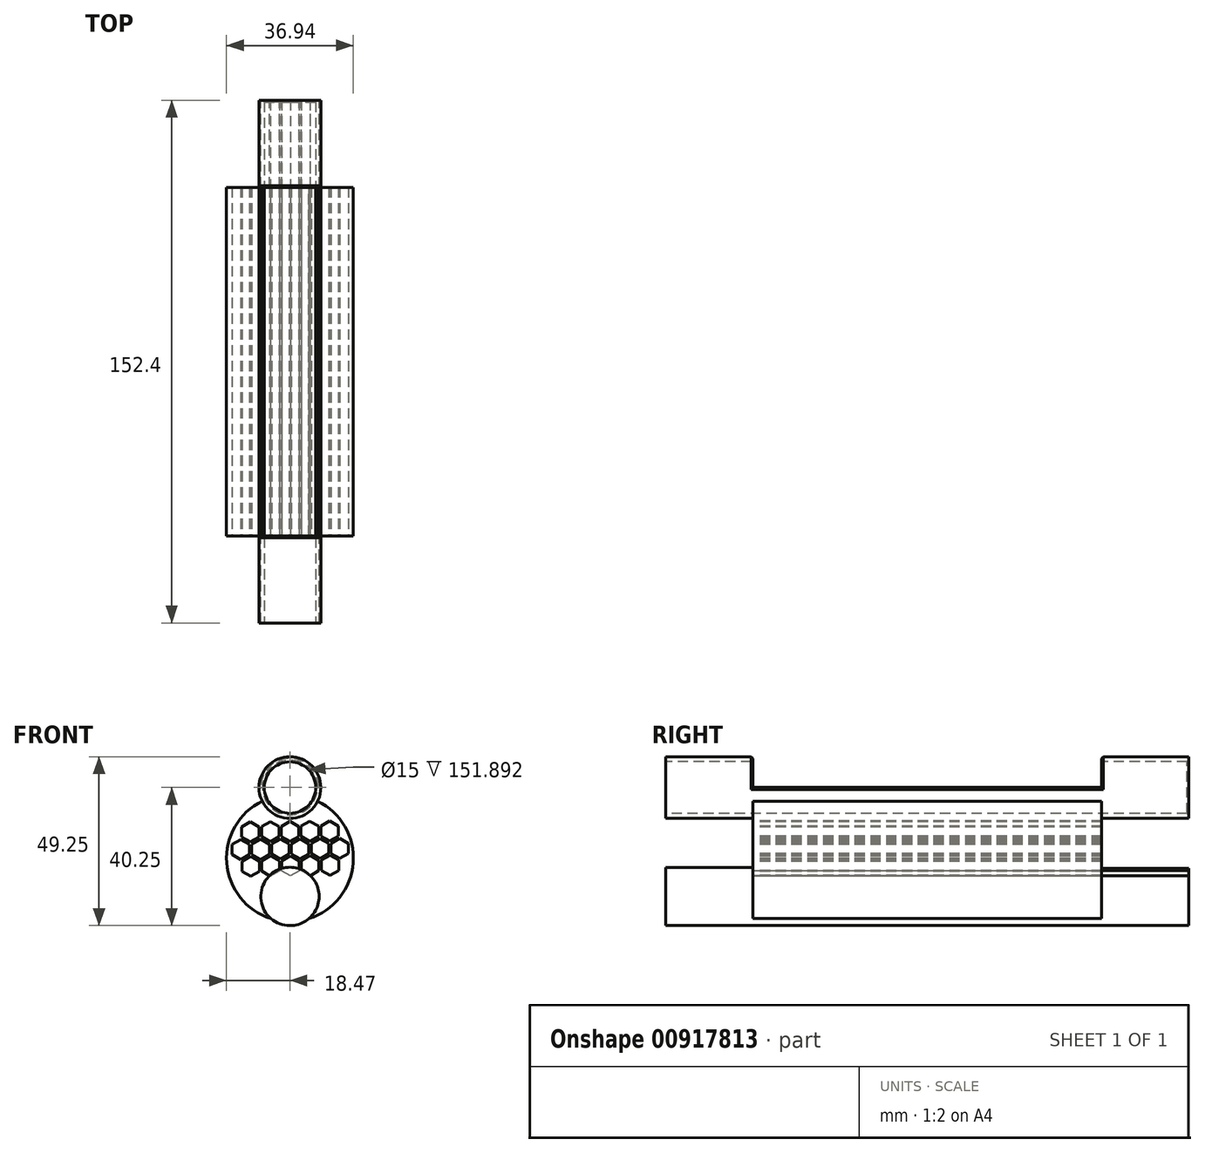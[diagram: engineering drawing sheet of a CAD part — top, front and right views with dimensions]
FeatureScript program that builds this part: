
annotation { "Feature Type Name" : "Feature", "Feature Type Description" : "" }
export const myFeature = defineFeature(function(context is Context, id is Id, definition is map)
    precondition{}
    {
        {
            var Q0;
            Q0=qCreatedBy(makeId("Front.planeOp"),FACE);
            var sketch = newSketch(context, id + "F0", { "sketchPlane" : qUnion([Q0])});
            skCircle(sketch, "E0", {"center": v(0, 0) * mm, "radius": 9 * mm});
            skCircle(sketch, "E1", {"center": v(0, -31.75) * mm, "radius": 8.5 * mm});
            skSolve(sketch);
        }
        {
            var Q0;
            Q0 = qSketchRegion(id + "FUGsYxlSOq7sT89_0", true);
            var Q1;
            Q1=makeQuery(id+"F0.imprint","IMPRINT",FACE,{"disambiguationData":[TD([[makeQuery(id+"F0.imprint","IMPRINT",EDGE,{"derivedFrom":sQuery(id+"F0.wireOp",EDGE,"E0")}),1.0]])]});
            var Q2;
            Q2=makeQuery(id+"F0.imprint","IMPRINT",FACE,{"disambiguationData":[TD([[makeQuery(id+"F0.imprint","IMPRINT",EDGE,{"derivedFrom":sQuery(id+"F0.wireOp",EDGE,"E1")}),1.0]])]});
            extrude(context, id + "F1", {"entities" : qUnion([Q0, Q1, Q2]), "endBound" : BoundingType.SYMMETRIC, "depth" : 152.4 * mm, "offsetDistance" : 25.4 * mm});
        }
        {
            var Q0;
            Q0=makeQuery(id+"F1.opExtrude","CAP_FACE",FACE,{"disambiguationData":[OSD([sQuery(id+"F0.wireOp",EDGE,"E0")])],"isStart":false});
            var sketch = newSketch(context, id + "F2", { "sketchPlane" : qUnion([Q0])});
            skCircle(sketch, "E2", {"center": v(0, 0) * mm, "radius": 7.5 * mm});
            skSolve(sketch);
        }
        {
            var Q0;
            Q0 = qSketchRegion(id + "F2", true);
            extrude(context, id + "F3", {"entities" : qUnion([Q0]), "operationType" : NewBodyOperationType.REMOVE, "endBound" : BoundingType.THROUGH_ALL, "oppositeDirection" : true, "depth" : 25.4 * mm, "offsetDistance" : 25.4 * mm});
        }
        {
            var Q0;
            Q0=makeQuery(id+"F0.imprint","IMPRINT",FACE,{"disambiguationData":[TD([[makeQuery(id+"F0.imprint","IMPRINT",EDGE,{"derivedFrom":sQuery(id+"F0.wireOp",EDGE,"E0")}),1.0]])]});
            var sketch = newSketch(context, id + "F4", { "sketchPlane" : qUnion([Q0])});
            skLineSegment(sketch, "E3.bottom", {"start": v(-11.18, 12.2) * mm, "end": v(12.33, 12.2) * mm});
            skLineSegment(sketch, "E3.top", {"start": v(-11.18, 0) * mm, "end": v(12.33, 0) * mm});
            skLineSegment(sketch, "E3.left", {"start": v(-11.18, 12.2) * mm, "end": v(-11.18, 0) * mm});
            skLineSegment(sketch, "E3.right", {"start": v(12.33, 12.2) * mm, "end": v(12.33, 0) * mm});
            skSolve(sketch);
        }
        {
            var Q0;
            Q0 = qSketchRegion(id + "F4", true);
            extrude(context, id + "F5", {"entities" : qUnion([Q0]), "operationType" : NewBodyOperationType.REMOVE, "endBound" : BoundingType.SYMMETRIC, "oppositeDirection" : true, "depth" : 101.6 * mm, "offsetDistance" : 25.4 * mm});
        }
        {
            var Q0;
            Q0=makeQuery(id+"F5.boolean.opBoolean","INTERSECT",EDGE,{"disambiguationData":[OD(0.0)],"derivedFrom":[makeQuery(id+"F1.opExtrude","SWEPT_FACE",FACE,{"disambiguationData":[OSD([sQuery(id+"F0.wireOp",EDGE,"E0")])]}),makeQuery(id+"F5.opExtrude","SWEPT_FACE",FACE,{"disambiguationData":[OSD([sQuery(id+"F4.wireOp",EDGE,"E3.top")])]})]});
            var Q1;
            Q1=makeQuery(id+"F5.boolean.opBoolean","INTERSECT",EDGE,{"disambiguationData":[OD(1.0)],"derivedFrom":[makeQuery(id+"F1.opExtrude","SWEPT_FACE",FACE,{"disambiguationData":[OSD([sQuery(id+"F0.wireOp",EDGE,"E0")])]}),makeQuery(id+"F5.opExtrude","SWEPT_FACE",FACE,{"disambiguationData":[OSD([sQuery(id+"F4.wireOp",EDGE,"E3.top")])]})]});
            var Q2;
            Q2=makeQuery(id+"F5.boolean.opBoolean","INTERSECT",EDGE,{"disambiguationData":[OD(1.0)],"derivedFrom":[makeQuery(id+"F3.boolean.opBoolean","COPY",FACE,{"derivedFrom":makeQuery(id+"F3.opExtrude","SWEPT_FACE",FACE,{"disambiguationData":[OSD([sQuery(id+"F2.wireOp",EDGE,"E2")])]})}),makeQuery(id+"F5.opExtrude","SWEPT_FACE",FACE,{"disambiguationData":[OSD([sQuery(id+"F4.wireOp",EDGE,"E3.top")])]})]});
            var Q3;
            Q3=makeQuery(id+"F5.boolean.opBoolean","INTERSECT",EDGE,{"disambiguationData":[OD(0.0)],"derivedFrom":[makeQuery(id+"F3.boolean.opBoolean","COPY",FACE,{"derivedFrom":makeQuery(id+"F3.opExtrude","SWEPT_FACE",FACE,{"disambiguationData":[OSD([sQuery(id+"F2.wireOp",EDGE,"E2")])]})}),makeQuery(id+"F5.opExtrude","SWEPT_FACE",FACE,{"disambiguationData":[OSD([sQuery(id+"F4.wireOp",EDGE,"E3.top")])]})]});
            var Q4;
            Q4=makeQuery(id+"F5.boolean.opBoolean","INTERSECT",EDGE,{"derivedFrom":[makeQuery(id+"F1.opExtrude","SWEPT_FACE",FACE,{"disambiguationData":[OSD([sQuery(id+"F0.wireOp",EDGE,"E0")])]}),makeQuery(id+"F5.opExtrude","CAP_FACE",FACE,{"disambiguationData":[OSD([sQuery(id+"F4.wireOp",EDGE,"E3.bottom"),sQuery(id+"F4.wireOp",EDGE,"E3.top"),sQuery(id+"F4.wireOp",EDGE,"E3.left"),sQuery(id+"F4.wireOp",EDGE,"E3.right")])],"isStart":true})]});
            var Q5;
            Q5=makeQuery(id+"F5.boolean.opBoolean","INTERSECT",EDGE,{"derivedFrom":[makeQuery(id+"F1.opExtrude","SWEPT_FACE",FACE,{"disambiguationData":[OSD([sQuery(id+"F0.wireOp",EDGE,"E0")])]}),makeQuery(id+"F5.opExtrude","CAP_FACE",FACE,{"disambiguationData":[OSD([sQuery(id+"F4.wireOp",EDGE,"E3.bottom"),sQuery(id+"F4.wireOp",EDGE,"E3.top"),sQuery(id+"F4.wireOp",EDGE,"E3.left"),sQuery(id+"F4.wireOp",EDGE,"E3.right")])],"isStart":false})]});
            var Q6;
            Q6=makeQuery(id+"F5.boolean.opBoolean","INTERSECT",EDGE,{"derivedFrom":[makeQuery(id+"F3.boolean.opBoolean","COPY",FACE,{"derivedFrom":makeQuery(id+"F3.opExtrude","SWEPT_FACE",FACE,{"disambiguationData":[OSD([sQuery(id+"F2.wireOp",EDGE,"E2")])]})}),makeQuery(id+"F5.opExtrude","CAP_FACE",FACE,{"disambiguationData":[OSD([sQuery(id+"F4.wireOp",EDGE,"E3.bottom"),sQuery(id+"F4.wireOp",EDGE,"E3.top"),sQuery(id+"F4.wireOp",EDGE,"E3.left"),sQuery(id+"F4.wireOp",EDGE,"E3.right")])],"isStart":false})]});
            var Q7;
            Q7=makeQuery(id+"F5.boolean.opBoolean","INTERSECT",EDGE,{"derivedFrom":[makeQuery(id+"F3.boolean.opBoolean","COPY",FACE,{"derivedFrom":makeQuery(id+"F3.opExtrude","SWEPT_FACE",FACE,{"disambiguationData":[OSD([sQuery(id+"F2.wireOp",EDGE,"E2")])]})}),makeQuery(id+"F5.opExtrude","CAP_FACE",FACE,{"disambiguationData":[OSD([sQuery(id+"F4.wireOp",EDGE,"E3.bottom"),sQuery(id+"F4.wireOp",EDGE,"E3.top"),sQuery(id+"F4.wireOp",EDGE,"E3.left"),sQuery(id+"F4.wireOp",EDGE,"E3.right")])],"isStart":true})]});
            var Q8;
            Q8=makeQuery(id+"F3.boolean.opBoolean","INTERSECT",EDGE,{"derivedFrom":[makeQuery(id+"F1.opExtrude","CAP_FACE",FACE,{"disambiguationData":[OSD([sQuery(id+"F0.wireOp",EDGE,"E0")])],"isStart":true}),makeQuery(id+"F3.opExtrude","SWEPT_FACE",FACE,{"disambiguationData":[OSD([sQuery(id+"F2.wireOp",EDGE,"E2")])]})]});
            var Q9;
            Q9=makeQuery(id+"F3.boolean.opBoolean","COPY",EDGE,{"derivedFrom":makeQuery(id+"F3.opExtrude","CAP_EDGE",EDGE,{"disambiguationData":[OSD([sQuery(id+"F2.wireOp",EDGE,"E2")])],"isStart":true})});
            chamfer(context, id + "F6", {"entities" : qUnion([Q0, Q1, Q2, Q3, Q4, Q5, Q6, Q7, Q8, Q9]), "width" : 0.5 * mm, "tangentPropagation" : true});
        }
        {
            var Q0;
            Q0=qCreatedBy(makeId("Front.planeOp"),FACE);
            var sketch = newSketch(context, id + "F7", { "sketchPlane" : qUnion([Q0])});
            skLineSegment(sketch, "E4.0", {"start": v(2, -31.75) * mm, "end": v(2, -8.64) * mm});
            skLineSegment(sketch, "E5.0", {"start": v(-2, -31.75) * mm, "end": v(-2, -8.64) * mm});
            skPoint(sketch, "E6.start.orphan", {"position": v(0, -31.75) * mm});
            skLineSegment(sketch, "E7", {"start": v(-2, -31.75) * mm, "end": v(2, -31.75) * mm});
            skLineSegment(sketch, "E8", {"start": v(2, -8.64) * mm, "end": v(-2, -8.64) * mm});
            skSolve(sketch);
        }
        {
            var Q0;
            Q0 = qSketchRegion(id + "F7", true);
            extrude(context, id + "F8", {"entities" : qUnion([Q0]), "operationType" : NewBodyOperationType.ADD, "endBound" : BoundingType.SYMMETRIC, "oppositeDirection" : true, "depth" : 101.6 * mm, "offsetDistance" : 25.4 * mm});
        }
        {
            var Q0;
            Q0=qCreatedBy(makeId("Front.planeOp"),FACE);
            var sketch = newSketch(context, id + "F9", { "sketchPlane" : qUnion([Q0])});
            skCircle(sketch, "E9", {"center": v(0, -20.58) * mm, "radius": 18.47 * mm});
            skSolve(sketch);
        }
        {
            var Q0;
            Q0 = qSketchRegion(id + "F9", true);
            extrude(context, id + "F10", {"entities" : qUnion([Q0]), "operationType" : NewBodyOperationType.ADD, "endBound" : BoundingType.SYMMETRIC, "depth" : 101.6 * mm, "offsetDistance" : 25.4 * mm});
        }
        {
            var Q0;
            Q0=makeQuery(id+"F0.imprint","IMPRINT",FACE,{"disambiguationData":[TD([[makeQuery(id+"F0.imprint","IMPRINT",EDGE,{"derivedFrom":sQuery(id+"F0.wireOp",EDGE,"E0")}),1.0]])]});
            var sketch = newSketch(context, id + "F11", { "sketchPlane" : qUnion([Q0])});
            skCircle(sketch, "E10", {"center": v(0, 0) * mm, "radius": 7.5 * mm});
            skSolve(sketch);
        }
        {
            var Q0;
            Q0 = qSketchRegion(id + "F11", true);
            extrude(context, id + "F12", {"entities" : qUnion([Q0]), "operationType" : NewBodyOperationType.REMOVE, "endBound" : BoundingType.SYMMETRIC, "oppositeDirection" : true, "depth" : 152.4 * mm, "offsetDistance" : 25.4 * mm});
        }
        {
            var Q0;
            Q0=makeQuery(id+"F10.boolean.opBoolean","MERGE",FACE,{"derivedFrom":[makeQuery(id+"F8.opExtrude","CAP_FACE",FACE,{"disambiguationData":[OSD([sQuery(id+"F7.wireOp",EDGE,"E4.0"),sQuery(id+"F7.wireOp",EDGE,"E5.0"),sQuery(id+"F7.wireOp",EDGE,"E7"),sQuery(id+"F7.wireOp",EDGE,"E8")])],"isStart":true}),makeQuery(id+"F10.opExtrude","CAP_FACE",FACE,{"disambiguationData":[OSD([sQuery(id+"F9.wireOp",EDGE,"E9")])],"isStart":false})]});
            var sketch = newSketch(context, id + "F13", { "sketchPlane" : qUnion([Q0])});
            skCircle(sketch, "E11.cCircle", {"center": v(-11.52, -12.94) * mm, "radius": 2.55 * mm, "construction": true});
            skLineSegment(sketch, "E11.0", {"start": v(-8.97, -11.46) * mm, "end": v(-8.97, -14.4) * mm});
            skLineSegment(sketch, "E11.1", {"start": v(-8.97, -14.4) * mm, "end": v(-11.52, -15.88) * mm});
            skLineSegment(sketch, "E11.2", {"start": v(-11.52, -15.88) * mm, "end": v(-14.07, -14.4) * mm});
            skLineSegment(sketch, "E11.3", {"start": v(-14.07, -14.4) * mm, "end": v(-14.07, -11.46) * mm});
            skLineSegment(sketch, "E11.4", {"start": v(-14.07, -11.46) * mm, "end": v(-11.52, -10) * mm});
            skLineSegment(sketch, "E11.5", {"start": v(-11.52, -10) * mm, "end": v(-8.97, -11.46) * mm});
            skPoint(sketch, "E11.0.midPoint", {"position": v(-8.97, -12.94) * mm});
            skLineSegment(sketch, "E12.1.0.0", {"start": v(-5.75, -9.92) * mm, "end": v(-3.2, -11.4) * mm});
            skLineSegment(sketch, "E12.1.0.1", {"start": v(-8.3, -11.4) * mm, "end": v(-5.75, -9.92) * mm});
            skLineSegment(sketch, "E12.1.0.2", {"start": v(-8.3, -14.34) * mm, "end": v(-8.3, -11.4) * mm});
            skLineSegment(sketch, "E12.1.0.3", {"start": v(-5.75, -15.81) * mm, "end": v(-8.3, -14.34) * mm});
            skLineSegment(sketch, "E12.1.0.4", {"start": v(-3.2, -11.4) * mm, "end": v(-3.2, -14.34) * mm});
            skLineSegment(sketch, "E12.1.0.5", {"start": v(-3.2, -14.34) * mm, "end": v(-5.75, -15.81) * mm});
            skLineSegment(sketch, "E12.2.0.0", {"start": v(0.02, -9.85) * mm, "end": v(2.57, -11.33) * mm});
            skLineSegment(sketch, "E12.2.0.1", {"start": v(-2.53, -11.33) * mm, "end": v(0.02, -9.85) * mm});
            skLineSegment(sketch, "E12.2.0.2", {"start": v(-2.53, -14.27) * mm, "end": v(-2.53, -11.33) * mm});
            skLineSegment(sketch, "E12.2.0.3", {"start": v(0.02, -15.74) * mm, "end": v(-2.53, -14.27) * mm});
            skLineSegment(sketch, "E12.2.0.4", {"start": v(2.57, -11.33) * mm, "end": v(2.57, -14.27) * mm});
            skLineSegment(sketch, "E12.2.0.5", {"start": v(2.57, -14.27) * mm, "end": v(0.02, -15.74) * mm});
            skLineSegment(sketch, "E12.3.0.0", {"start": v(5.78, -9.79) * mm, "end": v(8.33, -11.26) * mm});
            skLineSegment(sketch, "E12.3.0.1", {"start": v(3.23, -11.26) * mm, "end": v(5.78, -9.79) * mm});
            skLineSegment(sketch, "E12.3.0.2", {"start": v(3.23, -14.2) * mm, "end": v(3.23, -11.26) * mm});
            skLineSegment(sketch, "E12.3.0.3", {"start": v(5.78, -15.67) * mm, "end": v(3.23, -14.2) * mm});
            skLineSegment(sketch, "E12.3.0.4", {"start": v(8.33, -11.26) * mm, "end": v(8.33, -14.2) * mm});
            skLineSegment(sketch, "E12.3.0.5", {"start": v(8.33, -14.2) * mm, "end": v(5.78, -15.67) * mm});
            skLineSegment(sketch, "E12.4.0.0", {"start": v(11.55, -9.72) * mm, "end": v(14.1, -11.19) * mm});
            skLineSegment(sketch, "E12.4.0.1", {"start": v(9, -11.19) * mm, "end": v(11.55, -9.72) * mm});
            skLineSegment(sketch, "E12.4.0.2", {"start": v(9, -14.13) * mm, "end": v(9, -11.19) * mm});
            skLineSegment(sketch, "E12.4.0.3", {"start": v(11.55, -15.6) * mm, "end": v(9, -14.13) * mm});
            skLineSegment(sketch, "E12.4.0.4", {"start": v(14.1, -11.19) * mm, "end": v(14.1, -14.13) * mm});
            skLineSegment(sketch, "E12.4.0.5", {"start": v(14.1, -14.13) * mm, "end": v(11.55, -15.6) * mm});
            skLineSegment(sketch, "E12.direction1", {"start": v(-11.52, -10) * mm, "end": v(-5.75, -9.92) * mm, "construction": true});
            skSolve(sketch);
        }
        {
            var Q0;
            Q0 = qSketchRegion(id + "F13", true);
            extrude(context, id + "F14", {"entities" : qUnion([Q0]), "operationType" : NewBodyOperationType.REMOVE, "oppositeDirection" : true, "depth" : 177.8 * mm, "offsetDistance" : 25.4 * mm});
        }
        {
            var Q0;
            Q0=makeQuery(id+"F10.boolean.opBoolean","MERGE",FACE,{"derivedFrom":[makeQuery(id+"F8.opExtrude","CAP_FACE",FACE,{"disambiguationData":[OSD([sQuery(id+"F7.wireOp",EDGE,"E4.0"),sQuery(id+"F7.wireOp",EDGE,"E5.0"),sQuery(id+"F7.wireOp",EDGE,"E7"),sQuery(id+"F7.wireOp",EDGE,"E8")])],"isStart":true}),makeQuery(id+"F10.opExtrude","CAP_FACE",FACE,{"disambiguationData":[OSD([sQuery(id+"F9.wireOp",EDGE,"E9")])],"isStart":false})]});
            var sketch = newSketch(context, id + "F15", { "sketchPlane" : qUnion([Q0])});
            skCircle(sketch, "E13.cCircle", {"center": v(-14.33, -18.09) * mm, "radius": 2.55 * mm, "construction": true});
            skLineSegment(sketch, "E13.0", {"start": v(-11.78, -16.61) * mm, "end": v(-11.78, -19.56) * mm});
            skLineSegment(sketch, "E13.1", {"start": v(-11.78, -19.56) * mm, "end": v(-14.33, -21.03) * mm});
            skLineSegment(sketch, "E13.2", {"start": v(-14.33, -21.03) * mm, "end": v(-16.88, -19.56) * mm});
            skLineSegment(sketch, "E13.3", {"start": v(-16.88, -19.56) * mm, "end": v(-16.88, -16.61) * mm});
            skLineSegment(sketch, "E13.4", {"start": v(-16.88, -16.61) * mm, "end": v(-14.33, -15.14) * mm});
            skLineSegment(sketch, "E13.5", {"start": v(-14.33, -15.14) * mm, "end": v(-11.78, -16.61) * mm});
            skPoint(sketch, "E13.0.midPoint", {"position": v(-11.78, -18.09) * mm});
            skLineSegment(sketch, "E14.1.0.0", {"start": v(-8.56, -15.07) * mm, "end": v(-6.01, -16.55) * mm});
            skLineSegment(sketch, "E14.1.0.1", {"start": v(-11.11, -16.55) * mm, "end": v(-8.56, -15.07) * mm});
            skLineSegment(sketch, "E14.1.0.2", {"start": v(-11.11, -19.5) * mm, "end": v(-11.11, -16.55) * mm});
            skLineSegment(sketch, "E14.1.0.3", {"start": v(-8.56, -20.96) * mm, "end": v(-11.11, -19.5) * mm});
            skLineSegment(sketch, "E14.1.0.4", {"start": v(-6.01, -16.55) * mm, "end": v(-6.01, -19.5) * mm});
            skLineSegment(sketch, "E14.1.0.5", {"start": v(-6.01, -19.5) * mm, "end": v(-8.56, -20.96) * mm});
            skLineSegment(sketch, "E14.2.0.0", {"start": v(-2.8, -15) * mm, "end": v(-0.25, -16.48) * mm});
            skLineSegment(sketch, "E14.2.0.1", {"start": v(-5.35, -16.48) * mm, "end": v(-2.8, -15) * mm});
            skLineSegment(sketch, "E14.2.0.2", {"start": v(-5.35, -19.42) * mm, "end": v(-5.35, -16.48) * mm});
            skLineSegment(sketch, "E14.2.0.3", {"start": v(-2.8, -20.9) * mm, "end": v(-5.35, -19.42) * mm});
            skLineSegment(sketch, "E14.2.0.4", {"start": v(-0.25, -16.48) * mm, "end": v(-0.25, -19.42) * mm});
            skLineSegment(sketch, "E14.2.0.5", {"start": v(-0.25, -19.42) * mm, "end": v(-2.8, -20.9) * mm});
            skLineSegment(sketch, "E14.3.0.0", {"start": v(2.97, -14.94) * mm, "end": v(5.52, -16.4) * mm});
            skLineSegment(sketch, "E14.3.0.1", {"start": v(0.42, -16.4) * mm, "end": v(2.97, -14.94) * mm});
            skLineSegment(sketch, "E14.3.0.2", {"start": v(0.42, -19.35) * mm, "end": v(0.42, -16.4) * mm});
            skLineSegment(sketch, "E14.3.0.3", {"start": v(2.97, -20.83) * mm, "end": v(0.42, -19.35) * mm});
            skLineSegment(sketch, "E14.3.0.4", {"start": v(5.52, -16.4) * mm, "end": v(5.52, -19.35) * mm});
            skLineSegment(sketch, "E14.3.0.5", {"start": v(5.52, -19.35) * mm, "end": v(2.97, -20.83) * mm});
            skLineSegment(sketch, "E14.4.0.0", {"start": v(8.73, -14.87) * mm, "end": v(11.28, -16.34) * mm});
            skLineSegment(sketch, "E14.4.0.1", {"start": v(6.18, -16.34) * mm, "end": v(8.73, -14.87) * mm});
            skLineSegment(sketch, "E14.4.0.2", {"start": v(6.18, -19.28) * mm, "end": v(6.18, -16.34) * mm});
            skLineSegment(sketch, "E14.4.0.3", {"start": v(8.73, -20.76) * mm, "end": v(6.18, -19.28) * mm});
            skLineSegment(sketch, "E14.4.0.4", {"start": v(11.28, -16.34) * mm, "end": v(11.28, -19.28) * mm});
            skLineSegment(sketch, "E14.4.0.5", {"start": v(11.28, -19.28) * mm, "end": v(8.73, -20.76) * mm});
            skLineSegment(sketch, "E14.direction1", {"start": v(-14.33, -15.14) * mm, "end": v(-8.56, -15.07) * mm, "construction": true});
            skLineSegment(sketch, "E15.0.5.0", {"start": v(14.5, -14.8) * mm, "end": v(17.05, -16.27) * mm});
            skLineSegment(sketch, "E15.3.5.0", {"start": v(11.95, -16.27) * mm, "end": v(14.5, -14.8) * mm});
            skLineSegment(sketch, "E15.6.5.0", {"start": v(11.95, -19.22) * mm, "end": v(11.95, -16.27) * mm});
            skLineSegment(sketch, "E15.9.5.0", {"start": v(14.5, -20.69) * mm, "end": v(11.95, -19.22) * mm});
            skLineSegment(sketch, "E15.12.5.0", {"start": v(17.05, -16.27) * mm, "end": v(17.05, -19.22) * mm});
            skLineSegment(sketch, "E15.15.5.0", {"start": v(17.05, -19.22) * mm, "end": v(14.5, -20.69) * mm});
            skSolve(sketch);
        }
        {
            var Q0;
            Q0 = qSketchRegion(id + "F15", true);
            extrude(context, id + "F16", {"entities" : qUnion([Q0]), "operationType" : NewBodyOperationType.REMOVE, "oppositeDirection" : true, "depth" : 177.8 * mm, "offsetDistance" : 25.4 * mm});
        }
        {
            var Q0;
            Q0=makeQuery(id+"F10.boolean.opBoolean","MERGE",FACE,{"derivedFrom":[makeQuery(id+"F8.opExtrude","CAP_FACE",FACE,{"disambiguationData":[OSD([sQuery(id+"F7.wireOp",EDGE,"E4.0"),sQuery(id+"F7.wireOp",EDGE,"E5.0"),sQuery(id+"F7.wireOp",EDGE,"E7"),sQuery(id+"F7.wireOp",EDGE,"E8")])],"isStart":true}),makeQuery(id+"F10.opExtrude","CAP_FACE",FACE,{"disambiguationData":[OSD([sQuery(id+"F9.wireOp",EDGE,"E9")])],"isStart":false})]});
            var sketch = newSketch(context, id + "F17", { "sketchPlane" : qUnion([Q0])});
            skCircle(sketch, "E16.cCircle", {"center": v(-11.41, -22.95) * mm, "radius": 2.55 * mm, "construction": true});
            skLineSegment(sketch, "E16.0", {"start": v(-8.86, -21.48) * mm, "end": v(-8.86, -24.43) * mm});
            skLineSegment(sketch, "E16.1", {"start": v(-8.86, -24.43) * mm, "end": v(-11.41, -25.9) * mm});
            skLineSegment(sketch, "E16.2", {"start": v(-11.41, -25.9) * mm, "end": v(-13.96, -24.43) * mm});
            skLineSegment(sketch, "E16.3", {"start": v(-13.96, -24.43) * mm, "end": v(-13.96, -21.48) * mm});
            skLineSegment(sketch, "E16.4", {"start": v(-13.96, -21.48) * mm, "end": v(-11.41, -20) * mm});
            skLineSegment(sketch, "E16.5", {"start": v(-11.41, -20) * mm, "end": v(-8.86, -21.48) * mm});
            skPoint(sketch, "E16.0.midPoint", {"position": v(-8.86, -22.95) * mm});
            skLineSegment(sketch, "E17.1.0.0", {"start": v(-5.65, -19.94) * mm, "end": v(-3.1, -21.41) * mm});
            skLineSegment(sketch, "E17.1.0.1", {"start": v(-8.2, -21.41) * mm, "end": v(-5.65, -19.94) * mm});
            skLineSegment(sketch, "E17.1.0.2", {"start": v(-8.2, -24.36) * mm, "end": v(-8.2, -21.41) * mm});
            skLineSegment(sketch, "E17.1.0.3", {"start": v(-5.65, -25.83) * mm, "end": v(-8.2, -24.36) * mm});
            skLineSegment(sketch, "E17.1.0.4", {"start": v(-3.1, -21.41) * mm, "end": v(-3.1, -24.36) * mm});
            skLineSegment(sketch, "E17.1.0.5", {"start": v(-3.1, -24.36) * mm, "end": v(-5.65, -25.83) * mm});
            skLineSegment(sketch, "E17.direction1", {"start": v(-11.41, -20) * mm, "end": v(-5.65, -19.94) * mm, "construction": true});
            skLineSegment(sketch, "E18.0.2.0", {"start": v(0.12, -19.87) * mm, "end": v(2.67, -21.34) * mm});
            skLineSegment(sketch, "E18.3.2.0", {"start": v(-2.43, -21.34) * mm, "end": v(0.12, -19.87) * mm});
            skLineSegment(sketch, "E18.6.2.0", {"start": v(-2.43, -24.29) * mm, "end": v(-2.43, -21.34) * mm});
            skLineSegment(sketch, "E18.9.2.0", {"start": v(0.12, -25.76) * mm, "end": v(-2.43, -24.29) * mm});
            skLineSegment(sketch, "E18.12.2.0", {"start": v(2.67, -21.34) * mm, "end": v(2.67, -24.29) * mm});
            skLineSegment(sketch, "E18.15.2.0", {"start": v(2.67, -24.29) * mm, "end": v(0.12, -25.76) * mm});
            skLineSegment(sketch, "E18.0.3.0", {"start": v(5.88, -19.8) * mm, "end": v(8.43, -21.28) * mm});
            skLineSegment(sketch, "E18.3.3.0", {"start": v(3.33, -21.28) * mm, "end": v(5.88, -19.8) * mm});
            skLineSegment(sketch, "E18.6.3.0", {"start": v(3.33, -24.22) * mm, "end": v(3.33, -21.28) * mm});
            skLineSegment(sketch, "E18.9.3.0", {"start": v(5.88, -25.7) * mm, "end": v(3.33, -24.22) * mm});
            skLineSegment(sketch, "E18.12.3.0", {"start": v(8.43, -21.28) * mm, "end": v(8.43, -24.22) * mm});
            skLineSegment(sketch, "E18.15.3.0", {"start": v(8.43, -24.22) * mm, "end": v(5.88, -25.7) * mm});
            skLineSegment(sketch, "E18.0.4.0", {"start": v(11.65, -19.73) * mm, "end": v(14.2, -21.2) * mm});
            skLineSegment(sketch, "E18.3.4.0", {"start": v(9.1, -21.2) * mm, "end": v(11.65, -19.73) * mm});
            skLineSegment(sketch, "E18.6.4.0", {"start": v(9.1, -24.15) * mm, "end": v(9.1, -21.2) * mm});
            skLineSegment(sketch, "E18.9.4.0", {"start": v(11.65, -25.62) * mm, "end": v(9.1, -24.15) * mm});
            skLineSegment(sketch, "E18.12.4.0", {"start": v(14.2, -21.2) * mm, "end": v(14.2, -24.15) * mm});
            skLineSegment(sketch, "E18.15.4.0", {"start": v(14.2, -24.15) * mm, "end": v(11.65, -25.62) * mm});
            skSolve(sketch);
        }
        {
            var Q0;
            Q0 = qSketchRegion(id + "F17", true);
            extrude(context, id + "F18", {"entities" : qUnion([Q0]), "operationType" : NewBodyOperationType.REMOVE, "endBound" : BoundingType.THROUGH_ALL, "oppositeDirection" : true, "depth" : 25.4 * mm, "offsetDistance" : 25.4 * mm});
        }
    });
